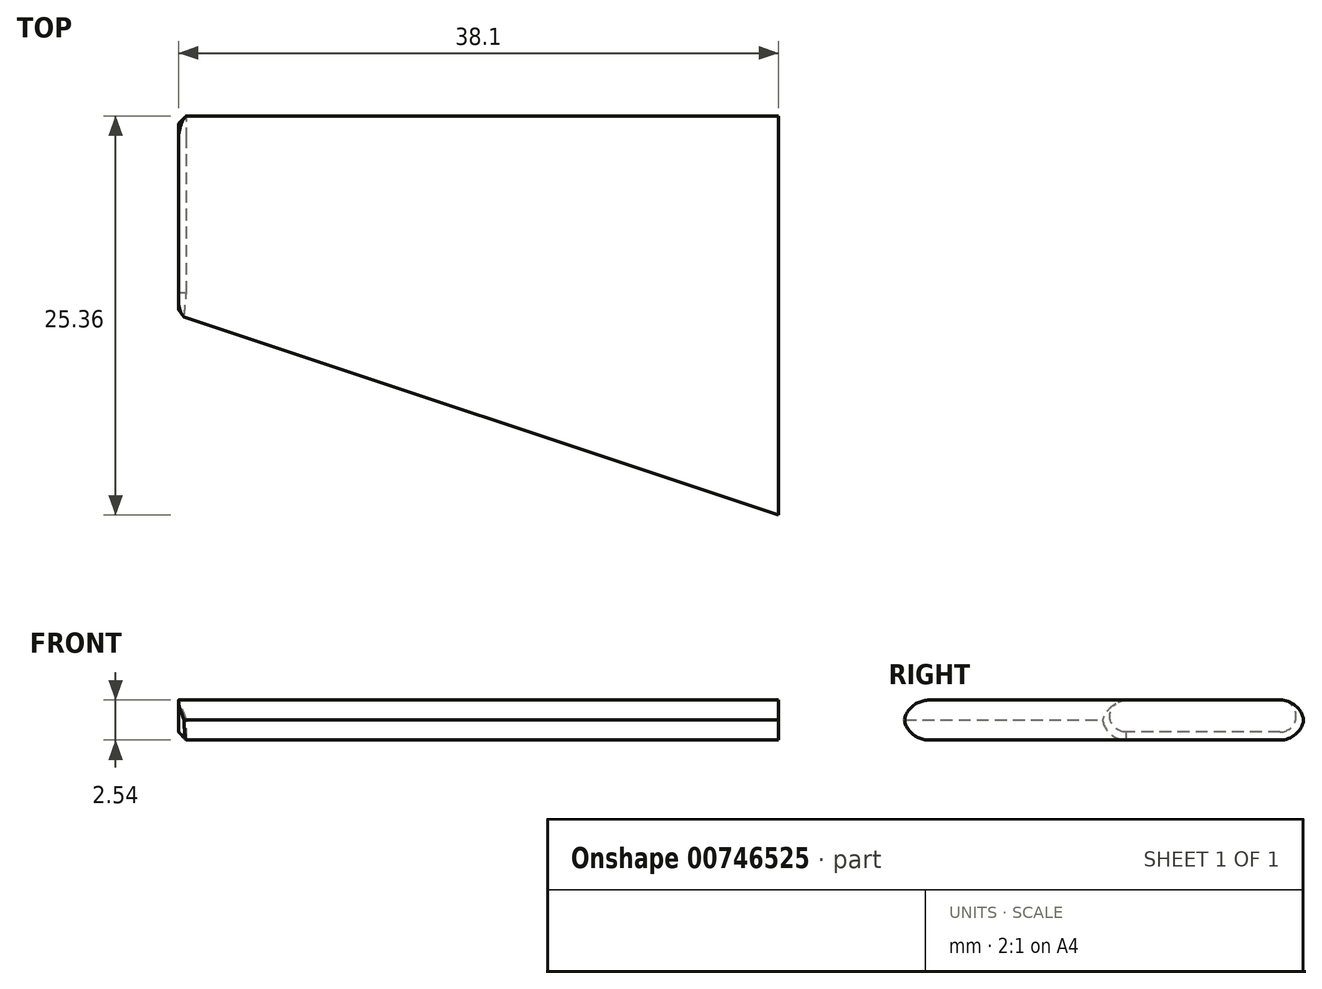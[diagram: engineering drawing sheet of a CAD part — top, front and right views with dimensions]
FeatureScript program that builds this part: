
annotation { "Feature Type Name" : "Feature", "Feature Type Description" : "" }
export const myFeature = defineFeature(function(context is Context, id is Id, definition is map)
    precondition{}
    {
        {
            var Q0;
            Q0=qCreatedBy(makeId("Top.planeOp"),FACE);
            var sketch = newSketch(context, id + "F0", { "sketchPlane" : qUnion([Q0])});
            skLineSegment(sketch, "E0", {"start": v(0, -44.38) * mm, "end": v(0, -18.98) * mm});
            skLineSegment(sketch, "E1", {"start": v(0, -18.98) * mm, "end": v(-38.1, -18.98) * mm});
            skLineSegment(sketch, "E2", {"start": v(-38.1, -18.98) * mm, "end": v(-38.1, -31.68) * mm});
            skLineSegment(sketch, "E3", {"start": v(-38.1, -31.68) * mm, "end": v(0, -44.38) * mm});
            skSolve(sketch);
        }
        {
            var Q0;
            Q0=makeQuery(id+"F0.imprint","IMPRINT",FACE,{"disambiguationData":[TD([[makeQuery(id+"F0.imprint","IMPRINT",EDGE,{"derivedFrom":sQuery(id+"F0.wireOp",EDGE,"E0")}),1.0]])]});
            extrude(context, id + "F1", {"entities" : qUnion([Q0]), "depth" : 2.54 * mm, "offsetDistance" : 25.4 * mm});
        }
        {
            var Q0;
            Q0=makeQuery(id+"F1.opExtrude","CAP_EDGE",EDGE,{"disambiguationData":[OSD([sQuery(id+"F0.wireOp",EDGE,"E1")])],"isStart":false});
            var Q1;
            Q1=makeQuery(id+"F1.opExtrude","CAP_EDGE",EDGE,{"disambiguationData":[OSD([sQuery(id+"F0.wireOp",EDGE,"E1")])],"isStart":true});
            var Q2;
            Q2=makeQuery(id+"F1.opExtrude","CAP_EDGE",EDGE,{"disambiguationData":[OSD([sQuery(id+"F0.wireOp",EDGE,"E3")])],"isStart":false});
            var Q3;
            Q3=makeQuery(id+"F1.opExtrude","CAP_EDGE",EDGE,{"disambiguationData":[OSD([sQuery(id+"F0.wireOp",EDGE,"E3")])],"isStart":true});
            fillet(context, id + "F2", {"entities" : qUnion([Q0, Q1, Q2, Q3]), "radius" : 1.52 * mm, "tangentPropagation" : true, "allowEdgeOverflow" : false});
        }
        {
            var Q0;
            Q0=makeQuery(id+"F1.opExtrude","CAP_EDGE",EDGE,{"disambiguationData":[OSD([sQuery(id+"F0.wireOp",EDGE,"E2")])],"isStart":true});
            chamfer(context, id + "F3", {"entities" : qUnion([Q0]), "width" : 0.5 * mm, "tangentPropagation" : true});
        }
    });
